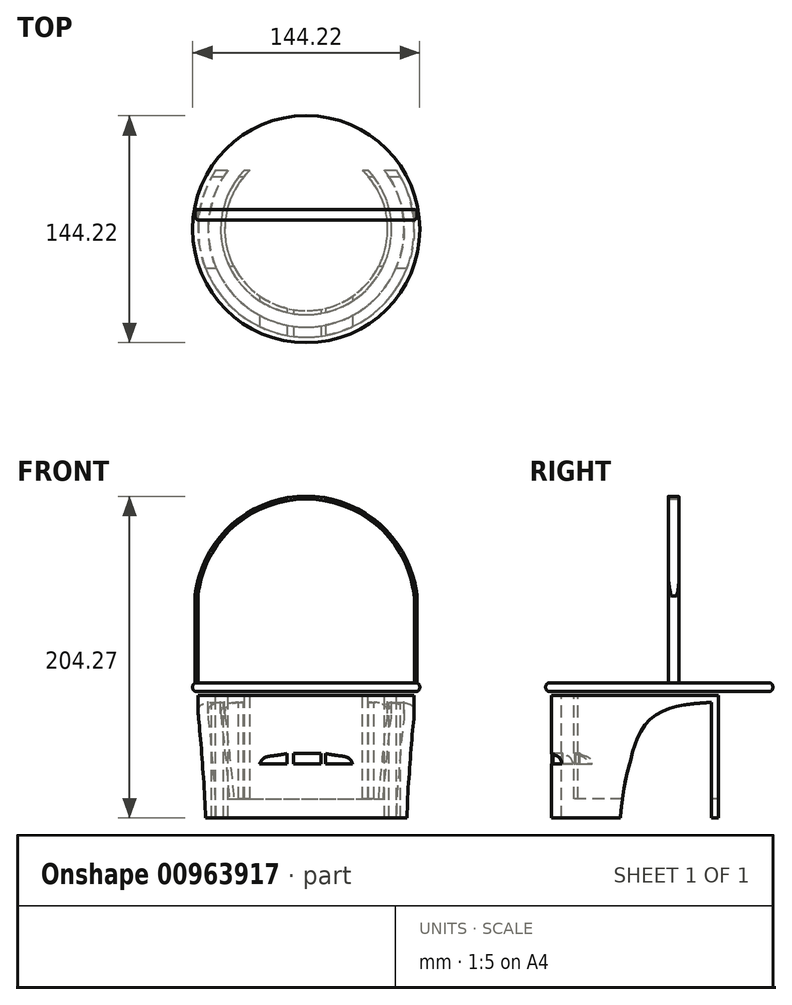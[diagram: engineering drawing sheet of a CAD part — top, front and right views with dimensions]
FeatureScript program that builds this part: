
annotation { "Feature Type Name" : "Feature", "Feature Type Description" : "" }
export const myFeature = defineFeature(function(context is Context, id is Id, definition is map)
    precondition{}
    {
        {
            var Q0;
            Q0=qCreatedBy(makeId("Front.planeOp"),FACE);
            var sketch = newSketch(context, id + "F0", { "sketchPlane" : qUnion([Q0])});
            skArc(sketch, "E0", {"start": v(0, 58.84) * mm, "mid": v(-41.89, 43.08) * mm, "end": v(-62.2, 3.2) * mm});
            skLineSegment(sketch, "E1", {"start": v(-62.2, 3.2) * mm, "end": v(-62.2, -77.42) * mm});
            skLineSegment(sketch, "E2", {"start": v(-62.2, -77.42) * mm, "end": v(-62.2, -135.57) * mm});
            skLineSegment(sketch, "E3.0", {"start": v(-68.55, -77.42) * mm, "end": v(-68.55, -135.57) * mm});
            skLineSegment(sketch, "E3.1", {"start": v(-68.55, 3.52) * mm, "end": v(-68.55, -77.42) * mm});
            skArc(sketch, "E3.2", {"start": v(0, 65.2) * mm, "mid": v(-46.27, 47.69) * mm, "end": v(-68.55, 3.52) * mm});
            skLineSegment(sketch, "E4", {"start": v(0, 58.84) * mm, "end": v(0, 65.2) * mm});
            skPoint(sketch, "E5.end.orphan", {"position": v(0, -77.42) * mm});
            skPoint(sketch, "E6.end.orphan", {"position": v(0, -135.57) * mm});
            skLineSegment(sketch, "E7", {"start": v(-62.2, -135.57) * mm, "end": v(-68.55, -135.57) * mm});
            skLineSegment(sketch, "E8", {"start": v(0, 111.47) * mm, "end": v(0, -172.38) * mm});
            skLineSegment(sketch, "E9", {"start": v(0, -123.39) * mm, "end": v(-54.28, -123.39) * mm});
            skLineSegment(sketch, "E10", {"start": v(-54.28, -123.39) * mm, "end": v(-54.28, -9.94) * mm});
            skArc(sketch, "E11", {"start": v(0, 44.37) * mm, "mid": v(-38.39, 28.45) * mm, "end": v(-54.28, -9.94) * mm});
            skSolve(sketch);
        }
        {
            var Q0;
            Q0 = qSketchRegion(id + "F0", true);
            var Q1;
            Q1=sQuery(id+"F0.wireOp",EDGE,"E8");
            revolve(context, id + "F1", {"surfaceOperationType" : NewSurfaceOperationType.NEW, "entities" : qUnion([Q0]), "axis" : qUnion([Q1]), "revolveType" : RevolveType.FULL});
        }
        {
            var Q0;
            Q0=qCreatedBy(makeId("Front.planeOp"),FACE);
            cPlane(context, id + "F2", {"entities" : qUnion([Q0]), "cplaneType" : CPlaneType.OFFSET, "offset" : 96.77 * mm, "width" : 152.4 * mm, "height" : 152.4 * mm});
        }
        {
            var Q0;
            Q0=qCreatedBy(id+"F2.planeOp",FACE);
            var sketch = newSketch(context, id + "F3", { "sketchPlane" : qUnion([Q0])});
            skLineSegment(sketch, "E12", {"start": v(-60.74, 0) * mm, "end": v(-60.74, -35.2) * mm});
            skLineSegment(sketch, "E13", {"start": v(-60.74, -35.2) * mm, "end": v(-15.72, -39.24) * mm});
            skLineSegment(sketch, "E14", {"start": v(-15.72, -39.24) * mm, "end": v(-15.72, -12.27) * mm});
            skLineSegment(sketch, "E15", {"start": v(-15.72, -12.27) * mm, "end": v(-60.74, 0) * mm});
            skLineSegment(sketch, "E16.MirrorCS", {"start": v(15.72, -12.27) * mm, "end": v(60.74, 0) * mm});
            skLineSegment(sketch, "E17.MirrorCS", {"start": v(15.72, -39.24) * mm, "end": v(15.72, -12.27) * mm});
            skLineSegment(sketch, "E18.MirrorCS", {"start": v(60.74, -35.2) * mm, "end": v(15.72, -39.24) * mm});
            skLineSegment(sketch, "E19.MirrorCS", {"start": v(60.74, 0) * mm, "end": v(60.74, -35.2) * mm});
            skLineSegment(sketch, "E20.bottom", {"start": v(-8.07, -94.67) * mm, "end": v(9.34, -94.67) * mm});
            skLineSegment(sketch, "E20.top", {"start": v(-8.07, -101.47) * mm, "end": v(9.34, -101.47) * mm});
            skLineSegment(sketch, "E20.left", {"start": v(-8.07, -94.67) * mm, "end": v(-8.07, -101.47) * mm});
            skLineSegment(sketch, "E20.right", {"start": v(9.34, -94.67) * mm, "end": v(9.34, -101.47) * mm});
            skLineSegment(sketch, "E21.top", {"start": v(-29.52, -101.47) * mm, "end": v(-12.1, -101.47) * mm});
            skLineSegment(sketch, "E21.right", {"start": v(-12.1, -94.67) * mm, "end": v(-12.1, -101.47) * mm});
            skFitSpline(sketch, "E22", {"points": [v(-29.52, -101.47) * mm, v(-27.82, -98.4) * mm, v(-24.8, -96.75) * mm, v(-18.86, -95.87) * mm, v(-12.1, -94.67) * mm], "startDerivative": vector(6.66, 15.92) * mm, "endDerivative": vector(22.62, 4.5) * mm});
            skFitSpline(sketch, "E23.MirrorCS", {"points": [v(29.52, -101.47) * mm, v(27.82, -98.4) * mm, v(24.8, -96.75) * mm, v(18.86, -95.87) * mm, v(12.1, -94.67) * mm], "startDerivative": vector(-6.66, 15.92) * mm, "endDerivative": vector(-22.62, 4.5) * mm});
            skLineSegment(sketch, "E24.MirrorCS", {"start": v(12.1, -94.67) * mm, "end": v(12.1, -101.47) * mm});
            skLineSegment(sketch, "E25.MirrorCS", {"start": v(29.52, -101.47) * mm, "end": v(12.1, -101.47) * mm});
            skSolve(sketch);
        }
        {
            var Q0;
            Q0=qCreatedBy(makeId("Right.planeOp"),FACE);
            var sketch = newSketch(context, id + "F4", { "sketchPlane" : qUnion([Q0])});
            skLineSegment(sketch, "E26", {"start": v(33.22, -138.02) * mm, "end": v(33.22, -62.2) * mm});
            skFitSpline(sketch, "E27", {"points": [v(33.22, -62.2) * mm, v(7.73, -65.82) * mm, v(-8.4, -75.8) * mm, v(-15.84, -90.24) * mm, v(-19.88, -105.32) * mm, v(-22.21, -115.09) * mm, v(-24.34, -131.86) * mm, v(-24.97, -139.3) * mm], "startDerivative": vector(-144.52, -9.57) * mm, "endDerivative": vector(-5.02, -64.36) * mm});
            skLineSegment(sketch, "E28", {"start": v(33.22, -138.02) * mm, "end": v(-24.97, -139.3) * mm});
            skSolve(sketch);
        }
        {
            var Q0;
            Q0=makeQuery(id+"F1.opRevolve","SWEPT_FACE",FACE,{"disambiguationData":[OSD([sQuery(id+"F0.wireOp",EDGE,"JwdKlPCu-S9b0-Ymsq-n8St-3TdImX2zllzu")])]});
            var Q1;
            Q1=makeQuery(id+"F1.opRevolve","SWEPT_FACE",FACE,{"disambiguationData":[OSD([sQuery(id+"F0.wireOp",EDGE,"E9")])]});
            shell(context, id + "F5", {"entities" : qUnion([Q0, Q1]), "thickness" : 2.54 * mm});
        }
        {
            var Q0;
            Q0=makeQuery(id+"F3.imprint","IMPRINT",FACE,{"disambiguationData":[TD([[makeQuery(id+"F3.imprint","IMPRINT",EDGE,{"derivedFrom":sQuery(id+"F3.wireOp",EDGE,"E12")}),1.0]])]});
            var Q1;
            Q1=makeQuery(id+"F3.imprint","IMPRINT",FACE,{"disambiguationData":[TD([[makeQuery(id+"F3.imprint","IMPRINT",EDGE,{"derivedFrom":sQuery(id+"F3.wireOp",EDGE,"E16.MirrorCS")}),-1.0]])]});
            extrude(context, id + "F6", {"entities" : qUnion([Q0, Q1]), "operationType" : NewBodyOperationType.REMOVE, "oppositeDirection" : true, "depth" : 86.1 * mm, "offsetDistance" : 25.4 * mm});
        }
        {
            var Q0;
            Q0=makeQuery(id+"F3.imprint","IMPRINT",FACE,{"disambiguationData":[TD([[makeQuery(id+"F3.imprint","IMPRINT",EDGE,{"derivedFrom":sQuery(id+"F3.wireOp",EDGE,"E21.top")}),1.0]])]});
            var Q1;
            Q1=makeQuery(id+"F3.imprint","IMPRINT",FACE,{"disambiguationData":[TD([[makeQuery(id+"F3.imprint","IMPRINT",EDGE,{"derivedFrom":sQuery(id+"F3.wireOp",EDGE,"E20.bottom")}),-1.0]])]});
            var Q2;
            Q2=makeQuery(id+"F3.imprint","IMPRINT",FACE,{"disambiguationData":[TD([[makeQuery(id+"F3.imprint","IMPRINT",EDGE,{"derivedFrom":sQuery(id+"F3.wireOp",EDGE,"E23.MirrorCS")}),1.0]])]});
            extrude(context, id + "F7", {"entities" : qUnion([Q0, Q1, Q2]), "operationType" : NewBodyOperationType.REMOVE, "oppositeDirection" : true, "depth" : 102.1 * mm, "offsetDistance" : 25.4 * mm});
        }
        {
            var Q0;
            Q0 = qSketchRegion(id + "F4", true);
            extrude(context, id + "F8", {"entities" : qUnion([Q0]), "operationType" : NewBodyOperationType.REMOVE, "endBound" : BoundingType.SYMMETRIC, "oppositeDirection" : true, "depth" : 223.52 * mm, "offsetDistance" : 25.4 * mm});
        }
        {
            var Q0;
            Q0=qCreatedBy(makeId("Right.planeOp"),FACE);
            var sketch = newSketch(context, id + "F9", { "sketchPlane" : qUnion([Q0])});
            skLineSegment(sketch, "E29", {"start": v(70.14, -137.13) * mm, "end": v(70.14, 73.91) * mm});
            skArc(sketch, "E30", {"start": v(70.14, 73.91) * mm, "mid": v(-19.95, 70.8) * mm, "end": v(-75.74, 0) * mm});
            skLineSegment(sketch, "E31", {"start": v(-75.74, 0) * mm, "end": v(-75.74, -57.75) * mm});
            skLineSegment(sketch, "E32", {"start": v(-75.74, -57.75) * mm, "end": v(37.46, -57.75) * mm});
            skLineSegment(sketch, "E33", {"start": v(37.46, -57.75) * mm, "end": v(37.46, -138.96) * mm});
            skLineSegment(sketch, "E34", {"start": v(37.46, -138.96) * mm, "end": v(70.14, -137.13) * mm});
            skSolve(sketch);
        }
        {
            var Q0;
            Q0=makeQuery(id+"F9.imprint","IMPRINT",FACE,{"disambiguationData":[TD([[makeQuery(id+"F9.imprint","IMPRINT",EDGE,{"derivedFrom":sQuery(id+"F9.wireOp",EDGE,"E29")}),1.0]])]});
            extrude(context, id + "F10", {"entities" : qUnion([Q0]), "operationType" : NewBodyOperationType.REMOVE, "endBound" : BoundingType.SYMMETRIC, "oppositeDirection" : true, "depth" : 294.13 * mm, "offsetDistance" : 25.4 * mm});
        }
        {
            var Q0;
            Q0=qCreatedBy(makeId("Top.planeOp"),FACE);
            cPlane(context, id + "F11", {"entities" : qUnion([Q0]), "cplaneType" : CPlaneType.OFFSET, "offset" : 52.58 * mm, "oppositeDirection" : true, "width" : 152.4 * mm, "height" : 152.4 * mm});
        }
        {
            var Q0;
            Q0=qCreatedBy(id+"F11.planeOp",FACE);
            var sketch = newSketch(context, id + "F12", { "sketchPlane" : qUnion([Q0])});
            skCircle(sketch, "E35", {"center": v(0, 0) * mm, "radius": 72.11 * mm});
            skSolve(sketch);
        }
        {
            var Q0;
            Q0=makeQuery(id+"F12.imprint","IMPRINT",FACE,{"disambiguationData":[TD([[makeQuery(id+"F12.imprint","IMPRINT",EDGE,{"derivedFrom":sQuery(id+"F12.wireOp",EDGE,"E35")}),1.0]])]});
            extrude(context, id + "F13", {"entities" : qUnion([Q0]), "operationType" : NewBodyOperationType.ADD, "endBound" : BoundingType.SYMMETRIC, "depth" : 5.6 * mm, "offsetDistance" : 25.4 * mm});
        }
        {
            var Q0;
            Q0=makeQuery(id+"F13.opExtrude","CAP_EDGE",EDGE,{"disambiguationData":[OSD([sQuery(id+"F12.wireOp",EDGE,"E35")])],"isStart":false});
            var Q1;
            Q1=makeQuery(id+"F13.opExtrude","CAP_EDGE",EDGE,{"disambiguationData":[OSD([sQuery(id+"F12.wireOp",EDGE,"E35")])],"isStart":true});
            fillet(context, id + "F14", {"entities" : qUnion([Q0, Q1]), "radius" : 2.45 * mm, "tangentPropagation" : true, "allowEdgeOverflow" : false});
        }
        {
            var Q0;
            Q0=qCreatedBy(makeId("Front.planeOp"),FACE);
            cPlane(context, id + "F15", {"entities" : qUnion([Q0]), "cplaneType" : CPlaneType.OFFSET, "offset" : 9.14 * mm, "oppositeDirection" : true, "width" : 152.4 * mm, "height" : 152.4 * mm});
        }
        {
            var Q0;
            Q0=qCreatedBy(id+"F15.planeOp",FACE);
            var sketch = newSketch(context, id + "F16", { "sketchPlane" : qUnion([Q0])});
            skLineSegment(sketch, "E36", {"start": v(70.4, -50) * mm, "end": v(70.4, 5.35) * mm});
            skArc(sketch, "E37", {"start": v(70.4, 5.35) * mm, "mid": v(-0.1, 68.7) * mm, "end": v(-70.62, 5.35) * mm});
            skLineSegment(sketch, "E38", {"start": v(-70.62, 5.35) * mm, "end": v(-70.62, -50) * mm});
            skArc(sketch, "E39.0", {"start": v(68.63, 5.25) * mm, "mid": v(-0.15, 66.92) * mm, "end": v(-68.85, 5.16) * mm});
            skLineSegment(sketch, "E39.1", {"start": v(68.63, -50) * mm, "end": v(68.63, 5.25) * mm});
            skLineSegment(sketch, "E40", {"start": v(70.4, -50) * mm, "end": v(68.63, -50) * mm});
            skLineSegment(sketch, "E41", {"start": v(-70.62, -50) * mm, "end": v(-68.85, -50) * mm});
            skLineSegment(sketch, "E42", {"start": v(-68.85, -50) * mm, "end": v(-68.85, 5.16) * mm});
            skSolve(sketch);
        }
        {
            var Q0;
            Q0=makeQuery(id+"F16.imprint","IMPRINT",FACE,{"disambiguationData":[TD([[makeQuery(id+"F16.imprint","IMPRINT",EDGE,{"derivedFrom":sQuery(id+"F16.wireOp",EDGE,"E36")}),1.0]])]});
            extrude(context, id + "F17", {"entities" : qUnion([Q0]), "operationType" : NewBodyOperationType.ADD, "endBound" : BoundingType.SYMMETRIC, "depth" : 6.6 * mm, "offsetDistance" : 25.4 * mm});
        }
        {
            var Q0;
            Q0=makeQuery(id+"F17.opExtrude","CAP_EDGE",EDGE,{"disambiguationData":[OSD([sQuery(id+"F16.wireOp",EDGE,"E36")])],"isStart":false});
            var Q1;
            Q1=makeQuery(id+"F17.opExtrude","CAP_EDGE",EDGE,{"disambiguationData":[OSD([sQuery(id+"F16.wireOp",EDGE,"E38")])],"isStart":false});
            fillet(context, id + "F18", {"entities" : qUnion([Q0, Q1]), "radius" : 2.45 * mm, "tangentPropagation" : true, "allowEdgeOverflow" : false});
        }
        {
            var Q0;
            Q0=makeQuery(id+"F17.opExtrude","CAP_EDGE",EDGE,{"disambiguationData":[OSD([sQuery(id+"F16.wireOp",EDGE,"E38")])],"isStart":true});
            var Q1;
            Q1=makeQuery(id+"F17.opExtrude","CAP_EDGE",EDGE,{"disambiguationData":[OSD([sQuery(id+"F16.wireOp",EDGE,"E36")])],"isStart":true});
            fillet(context, id + "F19", {"entities" : qUnion([Q0, Q1]), "radius" : 1.84 * mm, "tangentPropagation" : true, "allowEdgeOverflow" : false});
        }
    });
